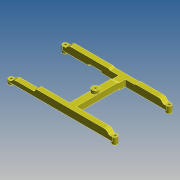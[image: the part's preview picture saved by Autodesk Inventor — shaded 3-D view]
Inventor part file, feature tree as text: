
AUTODESK INVENTOR PART (.ipt)
format: ipt  version: 2019 (Build 230136000, 136)  size: 360,448 bytes
history: native  units: mm
features: sketch x11, extrude x9, fillet x7, hole x2, projected_geometry x2
ambient origin geometry x8: Origin, YZ Plane, XZ Plane, XY Plane, X Axis, Y Axis, Z Axis, Center Point
bodies: Solid1 (feature_tree)
feature tree (31):
  extrude  "Corps"  Depth=6.0mm
  extrude  "Bossage pour vis"  Depth=6.0mm
  hole  "Hole1"  [1 undecoded]
  extrude  "Pieds"  Depth=9.0mm TaperAngle=0.0deg
  extrude  "Evidement sur pied 1"  Depth=4.0mm TaperAngle=0.0deg
  extrude  "Evidement sur pied 2"  Depth=3.0mm TaperAngle=0.0deg
  extrude  "Evidement dessous hor"  Depth=3.5mm TaperAngle=0.0deg
  hole  "Hole2"  [1 undecoded]
  fillet  "Fillet2"  Radius=50.0mm
  fillet  "Fillet5"  Radius=2.0mm
  fillet  "Fillet6"  Radius=9.0mm
  extrude  "Evidement dessus"  Depth=2.0mm
  fillet  "Fillet3"  Radius=65.66mm
  fillet  "Fillet4"  Radius=15.0mm
  extrude  "Evidement dessous 2"  Depth=1.0mm TaperAngle=0.0deg
  extrude  "Extrusion9"  Depth=2.0mm
  fillet  "Fillet7"  Radius=3.0mm
  fillet  "Fillet8"  Radius=6.0mm
  sketch  "Sketch1"  dims[d0=6.0mm d1=6.0mm]
  sketch  "Sketch2"  dims[d2=6.0mm d3=6.0mm]
  sketch  "Sketch3"  dims[d4=54.0mm d6=30.0mm]
  sketch  "Sketch5"  dims[d8=8.0mm d9=9.0mm d10=0.0mm]
  sketch  "Sketch6"  dims[d11=8.0mm d12=4.0mm d13=0.0mm]
  sketch  "Sketch7"  dims[d14=3.0mm d15=6.0mm d16=4.0mm d17=2.0mm d18=90.0deg d19=8.0mm d20=20.594885mm d21=3.0mm d22=0.0mm]
  sketch  "Sketch8"  dims[d23=32.0mm d24=3.5mm d25=0.0mm]
  sketch  "Sketch9"  dims[d26=3.5mm d27=0.0mm d29=35.0mm d30=50.0mm d31=2.0mm d32=9.0mm d33=0.0mm]
  sketch  "Sketch10"  dims[d34=3.3mm d35=6.0mm d36=4.0mm d37=2.0mm d38=90.0deg d39=8.0mm d40=20.594885mm d41=2.0mm d42=65.66mm d43=15.0mm]
  sketch  "Sketch11"  dims[d44=30.0mm d45=1.0mm d46=0.0mm]
  sketch  "Sketch12"  dims[d47=2.0mm d48=2.0mm d49=3.0mm d50=6.0mm d51=2.0mm d52=13.0mm d54=1.5mm d55=0.0mm d56=126.2mm d57=13.0mm d58=5.0mm d59=5.0mm d60=4.0mm d61=0.0mm d62=2.0mm d63=6.0mm]
  projected_geometry  "Project Cut Edges2"
  projected_geometry  "Project Cut Edges3"
note: 2 required parameter values undecoded (feature->parameter linkage not recoverable at this tier; creation-order binding heuristic only, values carry confidence <= 0.55)
